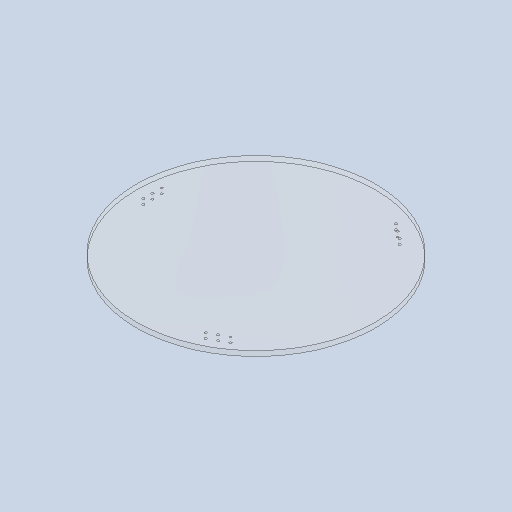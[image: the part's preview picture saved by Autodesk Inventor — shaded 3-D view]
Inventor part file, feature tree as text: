
AUTODESK INVENTOR PART (.ipt)
format: ipt  version: 2025.1 (Build 291241000, 241)  size: 270,848 bytes
history: native  units: mm
features: sketch x3, extrude x2
ambient origin geometry x8: Origin, YZ Plane, XZ Plane, XY Plane, X Axis, Y Axis, Z Axis, Center Point
bodies: Solid1 (feature_tree)
feature tree (5):
  sketch  "Sketch1"  dims[d20=300.0mm d22=120.0deg]
  extrude  "Extrusion1"  TaperAngle=120.0deg  [1 undecoded]
  extrude  "Extrusion3"  Depth=1.0mm
  sketch  "Sketch7"  dims[d25=10.33mm d26=20.066mm d27=3.0mm d28=20.066mm d29=3.0mm d30=20.066mm d31=3.0mm d32=6.35mm d33=0.0mm d36=10.0mm d37=10.0mm d38=3.0mm d39=3.0mm d40=10.0mm d41=10.0mm d42=3.0mm d43=3.0mm d44=10.0mm d45=10.0mm d46=3.0mm d47=3.0mm d48=0.0mm d49=0.0mm d34=0.5mm d35=0.872665mm d50=0.5mm d51=0.872665mm d52=0.5mm d53=0.872665mm]
  sketch  "Sketch2"  dims[d23=120.0deg d24=1.0mm]
note: 1 required parameter value undecoded (feature->parameter linkage not recoverable at this tier; creation-order binding heuristic only, values carry confidence <= 0.55)
